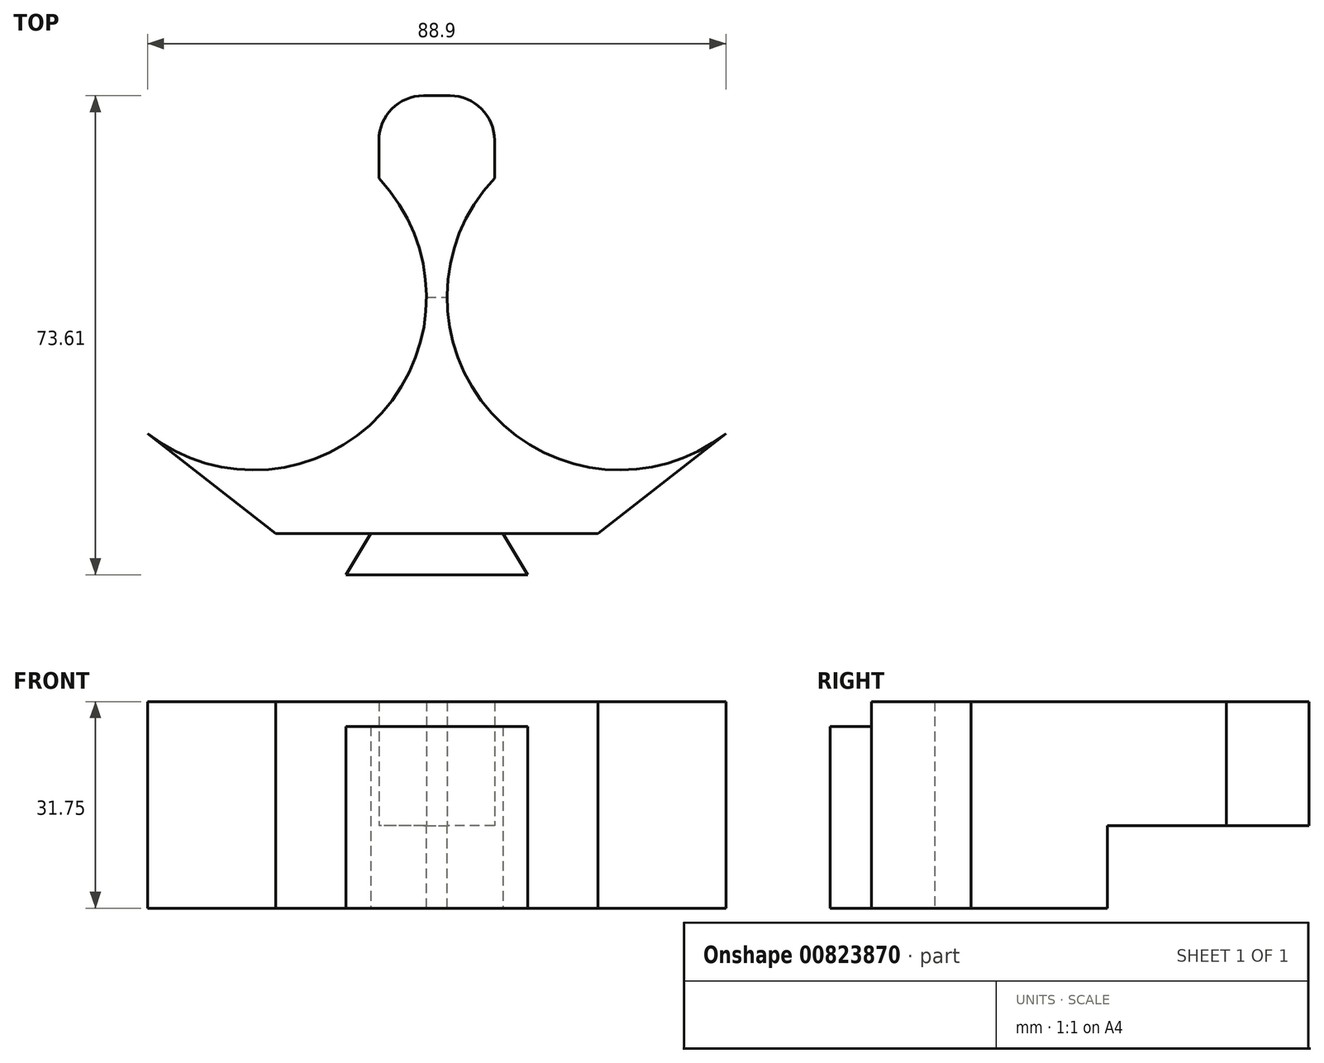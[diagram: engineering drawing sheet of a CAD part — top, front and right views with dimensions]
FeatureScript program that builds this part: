
annotation { "Feature Type Name" : "Feature", "Feature Type Description" : "" }
export const myFeature = defineFeature(function(context is Context, id is Id, definition is map)
    precondition{}
    {
        {
            var Q0;
            Q0=qCreatedBy(makeId("Top.planeOp"),FACE);
            var sketch = newSketch(context, id + "F0", { "sketchPlane" : qUnion([Q0])});
            skCircle(sketch, "E0", {"center": v(0, 0) * mm, "radius": 26.54 * mm});
            skCircle(sketch, "E1", {"center": v(56.26, 0) * mm, "radius": 26.54 * mm});
            skLineSegment(sketch, "E2", {"start": v(19.24, 18.28) * mm, "end": v(37.02, 18.28) * mm});
            skLineSegment(sketch, "E3", {"start": v(-16.32, -20.93) * mm, "end": v(-16.32, -36.28) * mm});
            skLineSegment(sketch, "E4", {"start": v(-16.32, -36.28) * mm, "end": v(72.58, -36.28) * mm});
            skLineSegment(sketch, "E5", {"start": v(72.58, -36.28) * mm, "end": v(72.58, -20.93) * mm});
            skLineSegment(sketch, "E6", {"start": v(28.13, 18.28) * mm, "end": v(28.13, -36.28) * mm, "construction": true});
            skPoint(sketch, "E6.endSnap0", {"position": v(28.13, -36.28) * mm});
            skLineSegment(sketch, "E7", {"start": v(-16.32, -20.93) * mm, "end": v(3.37, -36.28) * mm});
            skLineSegment(sketch, "E8", {"start": v(72.58, -20.93) * mm, "end": v(52.89, -36.28) * mm});
            skSolve(sketch);
        }
        {
            var Q0;
            {var subQ0=sQuery(id+"F0.wireOp",EDGE,"E2");Q0=makeQuery(id+"F0.imprint","IMPRINT",FACE,{"disambiguationData":[TD([[makeQuery(id+"F0.imprint","IMPRINT",EDGE,{"derivedFrom":subQ0}),-1.0]])]});}
            extrude(context, id + "F1", {"entities" : qUnion([Q0]), "depth" : 19.05 * mm, "offsetDistance" : 25.4 * mm});
        }
        {
            var Q0;
            Q0=makeQuery(id+"F1.opExtrude","CAP_FACE",FACE,{"disambiguationData":[OSD([sQuery(id+"F0.wireOp",EDGE,"E0"),sQuery(id+"F0.wireOp",EDGE,"E1"),sQuery(id+"F0.wireOp",EDGE,"E2"),sQuery(id+"F0.wireOp",EDGE,"E4"),sQuery(id+"F0.wireOp",EDGE,"E7"),sQuery(id+"F0.wireOp",EDGE,"E8")])],"isStart":true});
            var sketch = newSketch(context, id + "F2", { "sketchPlane" : qUnion([Q0])});
            skLineSegment(sketch, "E9", {"start": v(26.54, 0) * mm, "end": v(29.72, 0) * mm});
            skSolve(sketch);
        }
        {
            var Q0;
            {var subQ2=sQuery(id+"F2.wireOp",EDGE,"E9");Q0=makeQuery(id+"F2.imprint","IMPRINT",FACE,{"disambiguationData":[TD([[makeQuery(id+"F2.imprint","IMPRINT",EDGE,{"derivedFrom":subQ2}),1.0]])]});}
            extrude(context, id + "F3", {"entities" : qUnion([Q0]), "operationType" : NewBodyOperationType.ADD, "depth" : 12.7 * mm, "offsetDistance" : 25.4 * mm});
        }
        {
            var Q0;
            Q0=makeQuery(id+"F1.opExtrude","SWEPT_FACE",FACE,{"disambiguationData":[OSD([sQuery(id+"F0.wireOp",EDGE,"E2")])]});
            extrude(context, id + "F4", {"entities" : qUnion([Q0]), "operationType" : NewBodyOperationType.ADD, "depth" : 12.7 * mm, "offsetDistance" : 25.4 * mm});
        }
        {
            var Q0;
            {var subQ0=sQuery(id+"F0.wireOp",EDGE,"E4");Q0=makeQuery(id+"F3.boolean.opBoolean","MERGE",FACE,{"derivedFrom":[makeQuery(id+"F1.opExtrude","SWEPT_FACE",FACE,{"disambiguationData":[OSD([subQ0])]}),makeQuery(id+"F3.opExtrude","SWEPT_FACE",FACE,{"disambiguationData":[OSD([subQ0])]})]});}
            var sketch = newSketch(context, id + "F5", { "sketchPlane" : qUnion([Q0])});
            skLineSegment(sketch, "E10", {"start": v(28.13, -12.7) * mm, "end": v(28.13, 19.05) * mm, "construction": true});
            skLineSegment(sketch, "E11", {"start": v(42.1, -12.7) * mm, "end": v(42.1, 15.24) * mm});
            skLineSegment(sketch, "E12", {"start": v(42.1, 15.24) * mm, "end": v(14.16, 15.24) * mm});
            skLineSegment(sketch, "E13", {"start": v(14.16, 15.24) * mm, "end": v(14.16, -12.7) * mm});
            skPoint(sketch, "E14", {"position": v(28.13, 15.24) * mm});
            skLineSegment(sketch, "E15", {"start": v(38.3, -12.7) * mm, "end": v(38.3, 15.24) * mm});
            skLineSegment(sketch, "E16", {"start": v(17.97, -12.7) * mm, "end": v(17.97, 15.24) * mm});
            skSolve(sketch);
        }
        {
            var Q0;
            {var subQ0=sQuery(id+"F5.wireOp",EDGE,"E11");Q0=makeQuery(id+"F5.imprint","IMPRINT",FACE,{"disambiguationData":[TD([[makeQuery(id+"F5.imprint","IMPRINT",EDGE,{"derivedFrom":subQ0}),1.0]])]});}
            var Q1;
            {var subQ0=sQuery(id+"F5.wireOp",EDGE,"E15");Q1=makeQuery(id+"F5.imprint","IMPRINT",FACE,{"disambiguationData":[TD([[makeQuery(id+"F5.imprint","IMPRINT",EDGE,{"derivedFrom":subQ0}),1.0]])]});}
            var Q2;
            {var subQ0=sQuery(id+"F5.wireOp",EDGE,"E13");Q2=makeQuery(id+"F5.imprint","IMPRINT",FACE,{"disambiguationData":[TD([[makeQuery(id+"F5.imprint","IMPRINT",EDGE,{"derivedFrom":subQ0}),1.0]])]});}
            extrude(context, id + "F6", {"entities" : qUnion([Q0, Q1, Q2]), "operationType" : NewBodyOperationType.ADD, "depth" : 6.35 * mm, "offsetDistance" : 25.4 * mm});
        }
        {
            var Q0;
            {var subQ0=sQuery(id+"F0.wireOp",EDGE,"E4");Q0=makeQuery(id+"F6.boolean.opBoolean","MERGE",FACE,{"derivedFrom":[makeQuery(id+"F3.opExtrude","CAP_FACE",FACE,{"disambiguationData":[OSD([sQuery(id+"F0.wireOp",EDGE,"E0"),sQuery(id+"F0.wireOp",EDGE,"E1"),subQ0,sQuery(id+"F0.wireOp",EDGE,"E7"),sQuery(id+"F0.wireOp",EDGE,"E8"),sQuery(id+"F2.wireOp",EDGE,"E9")])],"isStart":false}),makeQuery(id+"F6.opExtrude","SWEPT_FACE",FACE,{"disambiguationData":[OSD([subQ0])]})]});}
            var sketch = newSketch(context, id + "F7", { "sketchPlane" : qUnion([Q0])});
            skLineSegment(sketch, "E17", {"start": v(38.3, 36.28) * mm, "end": v(42.1, 42.63) * mm});
            skLineSegment(sketch, "E18", {"start": v(14.16, 42.63) * mm, "end": v(17.97, 36.28) * mm});
            skLineSegment(sketch, "E19", {"start": v(38.3, 36.28) * mm, "end": v(42.1, 36.28) * mm});
            skLineSegment(sketch, "E20", {"start": v(42.1, 36.28) * mm, "end": v(42.1, 42.07) * mm});
            skLineSegment(sketch, "E21", {"start": v(17.97, 36.28) * mm, "end": v(14.16, 36.28) * mm});
            skLineSegment(sketch, "E22", {"start": v(14.16, 36.28) * mm, "end": v(14.16, 42.63) * mm});
            skSolve(sketch);
        }
        {
            var Q0;
            {var subQ0=sQuery(id+"F7.wireOp",EDGE,"E17");Q0=makeQuery(id+"F7.imprint","IMPRINT",FACE,{"disambiguationData":[TD([[makeQuery(id+"F7.imprint","IMPRINT",EDGE,{"derivedFrom":subQ0}),-1.0]])]});}
            var Q1;
            Q1=makeQuery(id+"F7.imprint","IMPRINT",FACE,{"disambiguationData":[TD([[makeQuery(id+"F7.imprint","IMPRINT",EDGE,{"derivedFrom":sQuery(id+"F7.wireOp",EDGE,"E18")}),-1.0]])]});
            extrude(context, id + "F8", {"entities" : qUnion([Q0, Q1]), "operationType" : NewBodyOperationType.REMOVE, "oppositeDirection" : true, "depth" : 40.4 * mm, "offsetDistance" : 25.4 * mm});
        }
        {
            var Q0;
            Q0=makeQuery(id+"F4.opExtrude","CAP_EDGE",EDGE,{"disambiguationData":[OSD([sQuery(id+"F0.wireOp",EDGE,"E1"),sQuery(id+"F0.wireOp",EDGE,"E2")])],"isStart":false});
            var Q1;
            Q1=makeQuery(id+"F4.opExtrude","CAP_EDGE",EDGE,{"disambiguationData":[OSD([sQuery(id+"F0.wireOp",EDGE,"E0"),sQuery(id+"F0.wireOp",EDGE,"E2")])],"isStart":false});
            fillet(context, id + "F9", {"entities" : qUnion([Q0, Q1]), "radius" : 6.86 * mm, "tangentPropagation" : true, "allowEdgeOverflow" : false});
        }
    });
